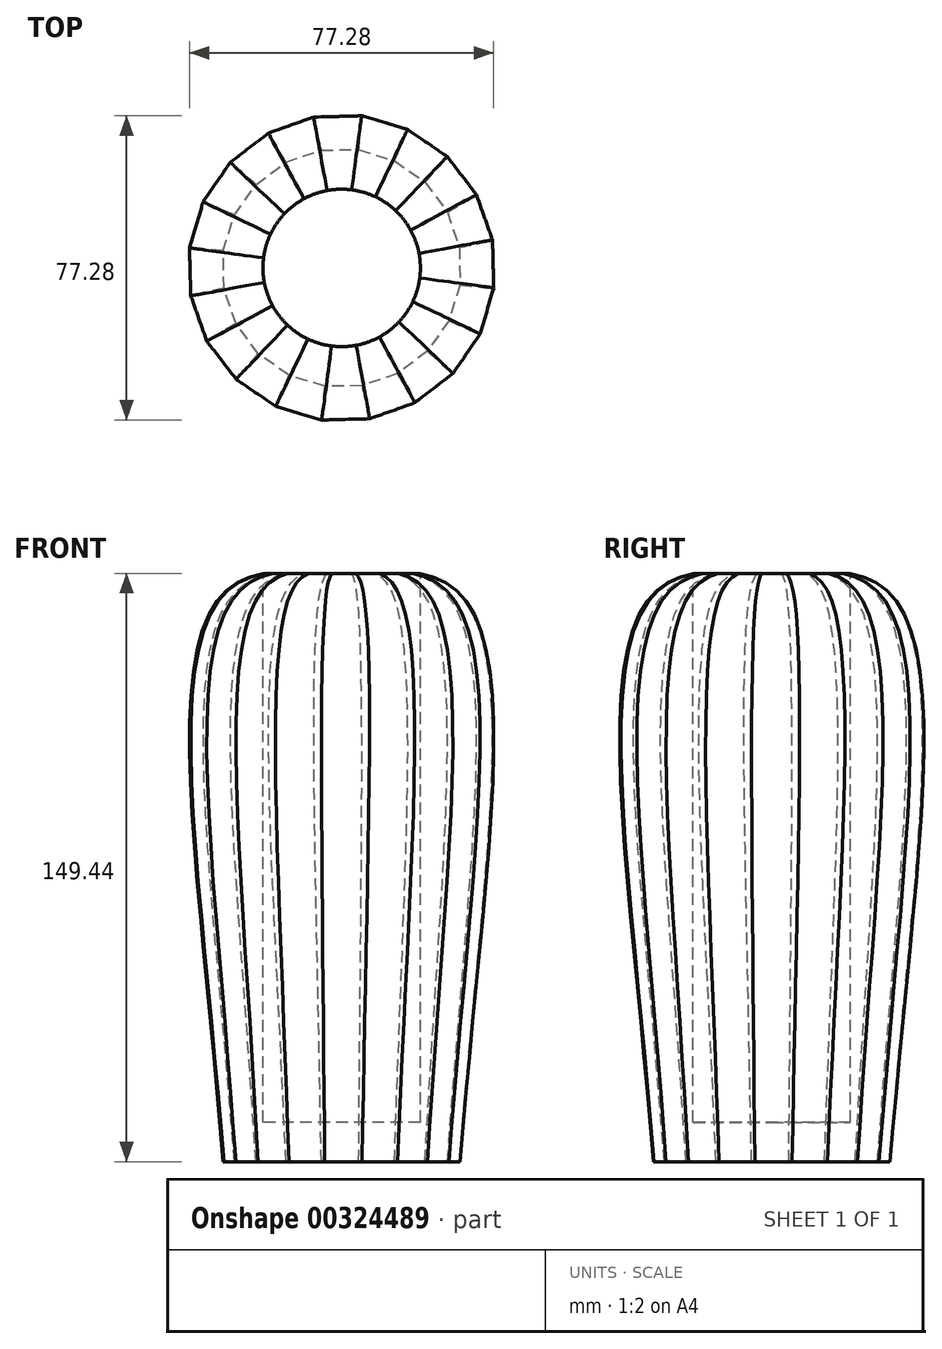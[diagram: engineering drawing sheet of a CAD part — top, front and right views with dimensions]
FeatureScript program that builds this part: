
annotation { "Feature Type Name" : "Feature", "Feature Type Description" : "" }
export const myFeature = defineFeature(function(context is Context, id is Id, definition is map)
    precondition{}
    {
        {
            var Q0;
            Q0=qCreatedBy(makeId("Top.planeOp"),FACE);
            var sketch = newSketch(context, id + "F0", { "sketchPlane" : qUnion([Q0])});
            skCircle(sketch, "E0", {"center": v(0, 0) * mm, "radius": 30 * mm});
            skCircle(sketch, "E1.cCircle", {"center": v(0, 0) * mm, "radius": 30 * mm, "construction": true});
            skLineSegment(sketch, "E1.0", {"start": v(4.33, 30.06) * mm, "end": v(13.41, 27.25) * mm});
            skLineSegment(sketch, "E1.1", {"start": v(13.41, 27.25) * mm, "end": v(21.18, 21.77) * mm});
            skLineSegment(sketch, "E1.2", {"start": v(21.18, 21.77) * mm, "end": v(26.87, 14.16) * mm});
            skLineSegment(sketch, "E1.3", {"start": v(26.87, 14.16) * mm, "end": v(29.93, 5.17) * mm});
            skLineSegment(sketch, "E1.4", {"start": v(29.93, 5.17) * mm, "end": v(30.06, -4.33) * mm});
            skLineSegment(sketch, "E1.5", {"start": v(30.06, -4.33) * mm, "end": v(27.25, -13.41) * mm});
            skLineSegment(sketch, "E1.6", {"start": v(27.25, -13.41) * mm, "end": v(21.77, -21.18) * mm});
            skLineSegment(sketch, "E1.7", {"start": v(21.77, -21.18) * mm, "end": v(14.16, -26.87) * mm});
            skLineSegment(sketch, "E1.8", {"start": v(14.16, -26.87) * mm, "end": v(5.17, -29.93) * mm});
            skLineSegment(sketch, "E1.9", {"start": v(5.17, -29.93) * mm, "end": v(-4.33, -30.06) * mm});
            skLineSegment(sketch, "E1.10", {"start": v(-4.33, -30.06) * mm, "end": v(-13.41, -27.25) * mm});
            skLineSegment(sketch, "E1.11", {"start": v(-13.41, -27.25) * mm, "end": v(-21.18, -21.77) * mm});
            skLineSegment(sketch, "E1.12", {"start": v(-21.18, -21.77) * mm, "end": v(-26.87, -14.16) * mm});
            skLineSegment(sketch, "E1.13", {"start": v(-26.87, -14.16) * mm, "end": v(-29.93, -5.17) * mm});
            skLineSegment(sketch, "E1.14", {"start": v(-29.93, -5.17) * mm, "end": v(-30.06, 4.33) * mm});
            skLineSegment(sketch, "E1.15", {"start": v(-30.06, 4.33) * mm, "end": v(-27.25, 13.41) * mm});
            skLineSegment(sketch, "E1.16", {"start": v(-27.25, 13.41) * mm, "end": v(-21.77, 21.18) * mm});
            skLineSegment(sketch, "E1.17", {"start": v(-21.77, 21.18) * mm, "end": v(-14.16, 26.87) * mm});
            skLineSegment(sketch, "E1.18", {"start": v(-14.16, 26.87) * mm, "end": v(-5.17, 29.93) * mm});
            skLineSegment(sketch, "E1.19", {"start": v(-5.17, 29.93) * mm, "end": v(4.33, 30.06) * mm});
            skPoint(sketch, "E1.0.midPoint", {"position": v(8.87, 28.66) * mm});
            skSolve(sketch);
        }
        {
            var Q0;
            Q0=qCreatedBy(makeId("Top.planeOp"),FACE);
            cPlane(context, id + "F1", {"entities" : qUnion([Q0]), "cplaneType" : CPlaneType.OFFSET, "offset" : 150 * mm, "width" : 150 * mm, "height" : 150 * mm});
        }
        {
            var Q0;
            Q0=qCreatedBy(id+"F1.planeOp",FACE);
            var sketch = newSketch(context, id + "F2", { "sketchPlane" : qUnion([Q0])});
            skCircle(sketch, "E2", {"center": v(0, 0) * mm, "radius": 10 * mm});
            skCircle(sketch, "E3.cCircle", {"center": v(0, 0) * mm, "radius": 10 * mm, "construction": true});
            skLineSegment(sketch, "E3.0", {"start": v(1.3, 10.04) * mm, "end": v(4.34, 9.15) * mm});
            skLineSegment(sketch, "E3.1", {"start": v(4.34, 9.15) * mm, "end": v(6.95, 7.36) * mm});
            skLineSegment(sketch, "E3.2", {"start": v(6.95, 7.36) * mm, "end": v(8.89, 4.85) * mm});
            skLineSegment(sketch, "E3.3", {"start": v(8.89, 4.85) * mm, "end": v(9.95, 1.87) * mm});
            skLineSegment(sketch, "E3.4", {"start": v(9.95, 1.87) * mm, "end": v(10.04, -1.3) * mm});
            skLineSegment(sketch, "E3.5", {"start": v(10.04, -1.3) * mm, "end": v(9.15, -4.34) * mm});
            skLineSegment(sketch, "E3.6", {"start": v(9.15, -4.34) * mm, "end": v(7.36, -6.95) * mm});
            skLineSegment(sketch, "E3.7", {"start": v(7.36, -6.95) * mm, "end": v(4.85, -8.89) * mm});
            skLineSegment(sketch, "E3.8", {"start": v(4.85, -8.89) * mm, "end": v(1.87, -9.95) * mm});
            skLineSegment(sketch, "E3.9", {"start": v(1.87, -9.95) * mm, "end": v(-1.3, -10.04) * mm});
            skLineSegment(sketch, "E3.10", {"start": v(-1.3, -10.04) * mm, "end": v(-4.34, -9.15) * mm});
            skLineSegment(sketch, "E3.11", {"start": v(-4.34, -9.15) * mm, "end": v(-6.95, -7.36) * mm});
            skLineSegment(sketch, "E3.12", {"start": v(-6.95, -7.36) * mm, "end": v(-8.89, -4.85) * mm});
            skLineSegment(sketch, "E3.13", {"start": v(-8.89, -4.85) * mm, "end": v(-9.95, -1.87) * mm});
            skLineSegment(sketch, "E3.14", {"start": v(-9.95, -1.87) * mm, "end": v(-10.04, 1.3) * mm});
            skLineSegment(sketch, "E3.15", {"start": v(-10.04, 1.3) * mm, "end": v(-9.15, 4.34) * mm});
            skLineSegment(sketch, "E3.16", {"start": v(-9.15, 4.34) * mm, "end": v(-7.36, 6.95) * mm});
            skLineSegment(sketch, "E3.17", {"start": v(-7.36, 6.95) * mm, "end": v(-4.85, 8.89) * mm});
            skLineSegment(sketch, "E3.18", {"start": v(-4.85, 8.89) * mm, "end": v(-1.87, 9.95) * mm});
            skLineSegment(sketch, "E3.19", {"start": v(-1.87, 9.95) * mm, "end": v(1.3, 10.04) * mm});
            skPoint(sketch, "E3.0.midPoint", {"position": v(2.82, 9.6) * mm});
            skSolve(sketch);
        }
        {
            var Q0;
            Q0 = qSketchRegion(id + "F0", true);
            var Q1;
            Q1 = qSketchRegion(id + "F2", true);
            loft(context, id + "F3", {"startCondition" : LoftEndDerivativeType.MATCH_CURVATURE, "startMagnitude" : 0, "endCondition" : LoftEndDerivativeType.MATCH_CURVATURE, "endMagnitude" : 3, "sheetProfilesArray" : [{ "sheetProfileEntities" : qUnion([Q0]) }, { "sheetProfileEntities" : qUnion([Q1]) }]});
        }
        {
            var Q0;
            {var subQ0=sQuery(id+"F2.wireOp",EDGE,"E2");var subQ8=makeQuery(id+"F2.imprint","INTERSECT",VERTEX,{"derivedFrom":[subQ0,sQuery(id+"F2.wireOp",EDGE,"E3.3")]});Q0=makeQuery(id+"F3.opLoft","CAP_FACE",FACE,{"disambiguationData":[OSD([makeQuery(id+"F2.imprint","IMPRINT",FACE,{"disambiguationData":[TD([[makeQuery(id+"F2.imprint","IMPRINT",EDGE,{"disambiguationData":[TD([[subQ8,1.0]])],"derivedFrom":subQ0}),1.0]])]})])],"isStart":true});}
            var sketch = newSketch(context, id + "F4", { "sketchPlane" : qUnion([Q0])});
            skCircle(sketch, "E4", {"center": v(0, 0) * mm, "radius": 20 * mm});
            skSolve(sketch);
        }
        {
            var Q0;
            {var subQ2=sQuery(id+"F2.wireOp",EDGE,"E2");var subQ8=sQuery(id+"F2.wireOp",EDGE,"E3.19");var subQ9=sQuery(id+"F2.wireOp",EDGE,"E3.0");Q0=makeQuery(id+"F4.imprint","IMPRINT",FACE,{"disambiguationData":[TD([[makeQuery(id+"F4.imprint","IMPRINT",EDGE,{"derivedFrom":makeQuery(id+"F3.opLoft","MID_CAP_EDGE",EDGE,{"disambiguationData":[OSD([subQ2,subQ9,subQ8])],"capPos":1.0})}),1.0]])]});}
            var Q1;
            Q1=makeQuery(id+"F4.imprint","IMPRINT",FACE,{"disambiguationData":[TD([[makeQuery(id+"F4.imprint","IMPRINT",EDGE,{"derivedFrom":sQuery(id+"F4.wireOp",EDGE,"E4")}),1.0]])]});
            extrude(context, id + "F5", {"entities" : qUnion([Q0, Q1]), "operationType" : NewBodyOperationType.REMOVE, "oppositeDirection" : true, "depth" : 140 * mm});
        }
    });
